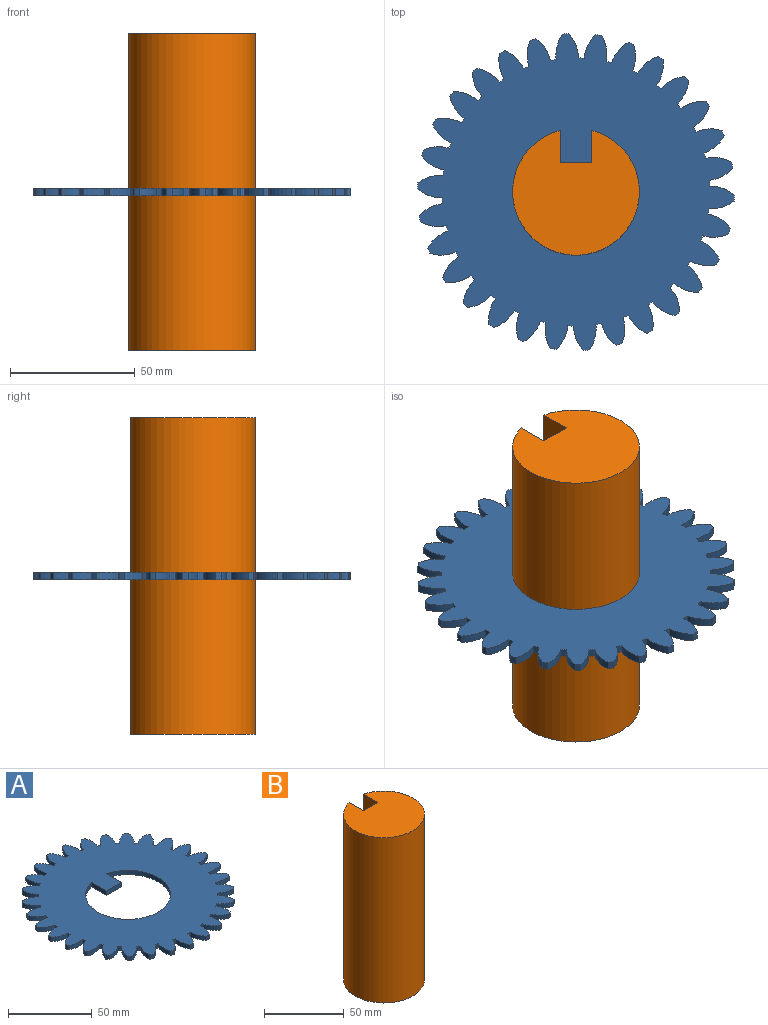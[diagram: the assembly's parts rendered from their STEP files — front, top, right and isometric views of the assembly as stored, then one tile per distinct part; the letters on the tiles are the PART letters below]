
ASSEMBLY  parts=2 mates=1
PART A: 126 faces, bbox 127x126.9x3.2 mm
  f0: cylinder r=25.4mm len=50.8mm, axis (0,0,-1), area 466mm2, adj f1,f123,f124,f125
  f1: plane 12.7x3.18mm, normal (-1,0,0), area 40.3mm2, adj f0,f2,f124,f125
  f2: plane 12.7x3.18mm, normal (0,-1,0), area 40.3mm2, adj f1,f123,f124,f125
  f3: cylinder r=14.61mm len=10.37mm, axis (0,0,-1), area 34.1mm2, adj f4,f122,f124,f125
  f4: cylinder r=53.72mm len=3.18mm, axis (0,0,-1), area 7.2mm2, adj f3,f5,f124,f125
  f5: cylinder r=14.61mm len=8.02mm, axis (0,0,-1), area 34.1mm2, adj f4,f6,f124,f125
  f6: cylinder r=63.5mm len=3.18mm, axis (0,0,-1), area 7.4mm2, adj f5,f7,f124,f125
  f7: cylinder r=14.61mm len=10.48mm, axis (0,0,-1), area 34.1mm2, adj f6,f8,f124,f125
  f8: cylinder r=53.72mm len=3.18mm, axis (0,0,-1), area 7.2mm2, adj f7,f9,f124,f125
  f9: cylinder r=14.61mm len=8.29mm, axis (0,0,-1), area 34.1mm2, adj f8,f10,f124,f125
  f10: cylinder r=63.5mm len=3.18mm, axis (0,0,-1), area 7.4mm2, adj f9,f11,f124,f125
  f11: cylinder r=14.61mm len=10.12mm, axis (0,0,-1), area 34.1mm2, adj f10,f12,f124,f125
  f12: cylinder r=53.72mm len=3.18mm, axis (0,0,-1), area 7.2mm2, adj f11,f13,f124,f125
  f13: cylinder r=14.61mm len=9.45mm, axis (0,0,-1), area 34.1mm2, adj f12,f14,f124,f125
  f14: cylinder r=63.5mm len=3.18mm, axis (0,0,-1), area 7.4mm2, adj f13,f15,f124,f125
  f15: cylinder r=14.61mm len=9.32mm, axis (0,0,-1), area 34.1mm2, adj f14,f16,f124,f125
  f16: cylinder r=53.72mm len=3.18mm, axis (0,0,-1), area 7.2mm2, adj f15,f17,f124,f125
  f17: cylinder r=14.61mm len=10.19mm, axis (0,0,-1), area 34.1mm2, adj f16,f18,f124,f125
  f18: cylinder r=63.5mm len=3.18mm, axis (0,0,-1), area 7.4mm2, adj f17,f19,f124,f125
  f19: cylinder r=14.61mm len=8.12mm, axis (0,0,-1), area 34.1mm2, adj f18,f20,f124,f125
  f20: cylinder r=53.72mm len=3.18mm, axis (0,0,-1), area 7.2mm2, adj f19,f21,f124,f125
  f21: cylinder r=14.61mm len=10.49mm, axis (0,0,-1), area 34.1mm2, adj f20,f22,f124,f125
  f22: cylinder r=63.5mm len=3.18mm, axis (0,0,-1), area 7.4mm2, adj f21,f23,f124,f125
  f23: cylinder r=14.61mm len=8.19mm, axis (0,0,-1), area 34.1mm2, adj f22,f24,f124,f125
  f24: cylinder r=53.72mm len=3.18mm, axis (0,0,-1), area 7.2mm2, adj f23,f25,f124,f125
  f25: cylinder r=14.61mm len=10.33mm, axis (0,0,-1), area 34.1mm2, adj f24,f26,f124,f125
  f26: cylinder r=63.5mm len=3.18mm, axis (0,0,-1), area 7.4mm2, adj f25,f27,f124,f125
  f27: cylinder r=14.61mm len=9.38mm, axis (0,0,-1), area 34.1mm2, adj f26,f28,f124,f125
  f28: cylinder r=53.72mm len=3.18mm, axis (0,0,-1), area 7.2mm2, adj f27,f29,f124,f125
  f29: cylinder r=14.61mm len=9.72mm, axis (0,0,-1), area 34.1mm2, adj f28,f30,f124,f125
  f30: cylinder r=63.5mm len=3.18mm, axis (0,0,-1), area 7.4mm2, adj f29,f31,f124,f125
  f31: cylinder r=14.61mm len=10.15mm, axis (0,0,-1), area 34.1mm2, adj f30,f32,f124,f125
  f32: cylinder r=53.72mm len=3.18mm, axis (0,0,-1), area 7.2mm2, adj f31,f33,f124,f125
  f33: cylinder r=14.61mm len=8.68mm, axis (0,0,-1), area 34.1mm2, adj f32,f34,f124,f125
  f34: cylinder r=63.5mm len=3.18mm, axis (0,0,-1), area 7.4mm2, adj f33,f35,f124,f125
  f35: cylinder r=14.61mm len=10.48mm, axis (0,0,-1), area 34.1mm2, adj f34,f36,f124,f125
  f36: cylinder r=53.72mm len=3.18mm, axis (0,0,-1), area 7.2mm2, adj f35,f37,f124,f125
  f37: cylinder r=14.61mm len=7.57mm, axis (0,0,-1), area 34.1mm2, adj f36,f38,f124,f125
  f38: cylinder r=63.5mm len=3.18mm, axis (0,0,-1), area 7.4mm2, adj f37,f39,f124,f125
  f39: cylinder r=14.61mm len=10.36mm, axis (0,0,-1), area 34.1mm2, adj f38,f40,f124,f125
  f40: cylinder r=53.72mm len=3.18mm, axis (0,0,-1), area 7.2mm2, adj f39,f41,f124,f125
  f41: cylinder r=14.61mm len=8.92mm, axis (0,0,-1), area 34.1mm2, adj f40,f42,f124,f125
  f42: cylinder r=63.5mm len=3.18mm, axis (0,0,-1), area 7.4mm2, adj f41,f43,f124,f125
  f43: cylinder r=14.61mm len=9.78mm, axis (0,0,-1), area 34.1mm2, adj f42,f44,f124,f125
  f44: cylinder r=53.72mm len=3.18mm, axis (0,0,-1), area 7.2mm2, adj f43,f45,f124,f125
  f45: cylinder r=14.61mm len=9.87mm, axis (0,0,-1), area 34.1mm2, adj f44,f46,f124,f125
  f46: cylinder r=63.5mm len=3.18mm, axis (0,0,-1), area 7.4mm2, adj f45,f47,f124,f125
  f47: cylinder r=14.61mm len=8.77mm, axis (0,0,-1), area 34.1mm2, adj f46,f48,f124,f125
  f48: cylinder r=53.72mm len=3.18mm, axis (0,0,-1), area 7.2mm2, adj f47,f49,f124,f125
  f49: cylinder r=14.61mm len=10.4mm, axis (0,0,-1), area 34.1mm2, adj f48,f50,f124,f125
  f50: cylinder r=63.5mm len=3.18mm, axis (0,0,-1), area 7.4mm2, adj f49,f51,f124,f125
  f51: cylinder r=14.61mm len=7.46mm, axis (0,0,-1), area 34.1mm2, adj f50,f52,f124,f125
  f52: cylinder r=53.72mm len=3.18mm, axis (0,0,-1), area 7.2mm2, adj f51,f53,f124,f125
  f53: cylinder r=14.61mm len=10.47mm, axis (0,0,-1), area 34.1mm2, adj f52,f54,f124,f125
  f54: cylinder r=63.5mm len=3.18mm, axis (0,0,-1), area 7.4mm2, adj f53,f55,f124,f125
  f55: cylinder r=14.61mm len=8.83mm, axis (0,0,-1), area 34.1mm2, adj f54,f56,f124,f125
  f56: cylinder r=53.72mm len=3.18mm, axis (0,0,-1), area 7.2mm2, adj f55,f57,f124,f125
  f57: cylinder r=14.61mm len=10.08mm, axis (0,0,-1), area 34.1mm2, adj f56,f58,f124,f125
  f58: cylinder r=63.5mm len=3.18mm, axis (0,0,-1), area 7.4mm2, adj f57,f59,f124,f125
  f59: cylinder r=14.61mm len=9.82mm, axis (0,0,-1), area 34.1mm2, adj f58,f60,f124,f125
  f60: cylinder r=53.72mm len=3.18mm, axis (0,0,-1), area 7.2mm2, adj f59,f61,f124,f125
  f61: cylinder r=14.61mm len=9.25mm, axis (0,0,-1), area 34.1mm2, adj f60,f62,f124,f125
  f62: cylinder r=63.5mm len=3.18mm, axis (0,0,-1), area 7.4mm2, adj f61,f63,f124,f125
  f63: cylinder r=14.61mm len=10.37mm, axis (0,0,-1), area 34.1mm2, adj f62,f64,f124,f125
  f64: cylinder r=53.72mm len=3.18mm, axis (0,0,-1), area 7.2mm2, adj f63,f65,f124,f125
  f65: cylinder r=14.61mm len=8.02mm, axis (0,0,-1), area 34.1mm2, adj f64,f66,f124,f125
  f66: cylinder r=63.5mm len=3.18mm, axis (0,0,-1), area 7.4mm2, adj f65,f67,f124,f125
  f67: cylinder r=14.61mm len=10.48mm, axis (0,0,-1), area 34.1mm2, adj f66,f68,f124,f125
  f68: cylinder r=53.72mm len=3.18mm, axis (0,0,-1), area 7.2mm2, adj f67,f69,f124,f125
  f69: cylinder r=14.61mm len=8.29mm, axis (0,0,-1), area 34.1mm2, adj f68,f70,f124,f125
  f70: cylinder r=63.5mm len=3.18mm, axis (0,0,-1), area 7.4mm2, adj f69,f71,f124,f125
  f71: cylinder r=14.61mm len=10.12mm, axis (0,0,-1), area 34.1mm2, adj f70,f72,f124,f125
  f72: cylinder r=53.72mm len=3.18mm, axis (0,0,-1), area 7.2mm2, adj f71,f73,f124,f125
  f73: cylinder r=14.61mm len=9.45mm, axis (0,0,-1), area 34.1mm2, adj f72,f74,f124,f125
  f74: cylinder r=63.5mm len=3.18mm, axis (0,0,-1), area 7.4mm2, adj f73,f75,f124,f125
  f75: cylinder r=14.61mm len=9.32mm, axis (0,0,-1), area 34.1mm2, adj f74,f76,f124,f125
  f76: cylinder r=53.72mm len=3.18mm, axis (0,0,-1), area 7.2mm2, adj f75,f77,f124,f125
  f77: cylinder r=14.61mm len=10.19mm, axis (0,0,-1), area 34.1mm2, adj f76,f78,f124,f125
  f78: cylinder r=63.5mm len=3.18mm, axis (0,0,-1), area 7.4mm2, adj f77,f79,f124,f125
  f79: cylinder r=14.61mm len=8.12mm, axis (0,0,-1), area 34.1mm2, adj f78,f80,f124,f125
  f80: cylinder r=53.72mm len=3.18mm, axis (0,0,-1), area 7.2mm2, adj f79,f81,f124,f125
  f81: cylinder r=14.61mm len=10.49mm, axis (0,0,-1), area 34.1mm2, adj f80,f82,f124,f125
  f82: cylinder r=63.5mm len=3.18mm, axis (0,0,-1), area 7.4mm2, adj f81,f83,f124,f125
  f83: cylinder r=14.61mm len=8.19mm, axis (0,0,-1), area 34.1mm2, adj f82,f84,f124,f125
  f84: cylinder r=53.72mm len=3.18mm, axis (0,0,-1), area 7.2mm2, adj f83,f85,f124,f125
  f85: cylinder r=14.61mm len=10.33mm, axis (0,0,-1), area 34.1mm2, adj f84,f86,f124,f125
  f86: cylinder r=63.5mm len=3.18mm, axis (0,0,-1), area 7.4mm2, adj f85,f87,f124,f125
  f87: cylinder r=14.61mm len=9.38mm, axis (0,0,-1), area 34.1mm2, adj f86,f88,f124,f125
  f88: cylinder r=53.72mm len=3.18mm, axis (0,0,-1), area 7.2mm2, adj f87,f89,f124,f125
  f89: cylinder r=14.61mm len=9.72mm, axis (0,0,-1), area 34.1mm2, adj f88,f90,f124,f125
  f90: cylinder r=63.5mm len=3.18mm, axis (0,0,-1), area 7.4mm2, adj f89,f91,f124,f125
  f91: cylinder r=14.61mm len=10.15mm, axis (0,0,-1), area 34.1mm2, adj f90,f92,f124,f125
  f92: cylinder r=53.72mm len=3.18mm, axis (0,0,-1), area 7.2mm2, adj f91,f93,f124,f125
  f93: cylinder r=14.61mm len=8.68mm, axis (0,0,-1), area 34.1mm2, adj f92,f94,f124,f125
  f94: cylinder r=63.5mm len=3.18mm, axis (0,0,-1), area 7.4mm2, adj f93,f95,f124,f125
  f95: cylinder r=14.61mm len=10.48mm, axis (0,0,-1), area 34.1mm2, adj f94,f96,f124,f125
  f96: cylinder r=53.72mm len=3.18mm, axis (0,0,-1), area 7.2mm2, adj f95,f97,f124,f125
  f97: cylinder r=14.61mm len=7.57mm, axis (0,0,-1), area 34.1mm2, adj f96,f98,f124,f125
  f98: cylinder r=63.5mm len=3.18mm, axis (0,0,-1), area 7.4mm2, adj f97,f99,f124,f125
  f99: cylinder r=14.61mm len=10.36mm, axis (0,0,-1), area 34.1mm2, adj f98,f100,f124,f125
  f100: cylinder r=53.72mm len=3.18mm, axis (0,0,-1), area 7.2mm2, adj f99,f101,f124,f125
  f101: cylinder r=14.61mm len=8.92mm, axis (0,0,-1), area 34.1mm2, adj f100,f102,f124,f125
  f102: cylinder r=63.5mm len=3.18mm, axis (0,0,-1), area 7.4mm2, adj f101,f103,f124,f125
  f103: cylinder r=14.61mm len=9.78mm, axis (0,0,-1), area 34.1mm2, adj f102,f104,f124,f125
  f104: cylinder r=53.72mm len=3.18mm, axis (0,0,-1), area 7.2mm2, adj f103,f105,f124,f125
  f105: cylinder r=14.61mm len=9.87mm, axis (0,0,-1), area 34.1mm2, adj f104,f106,f124,f125
  f106: cylinder r=63.5mm len=3.18mm, axis (0,0,-1), area 7.4mm2, adj f105,f107,f124,f125
  f107: cylinder r=14.61mm len=8.77mm, axis (0,0,-1), area 34.1mm2, adj f106,f108,f124,f125
  f108: cylinder r=53.72mm len=3.18mm, axis (0,0,-1), area 7.2mm2, adj f107,f109,f124,f125
  f109: cylinder r=14.61mm len=10.4mm, axis (0,0,-1), area 34.1mm2, adj f108,f110,f124,f125
  f110: cylinder r=63.5mm len=3.18mm, axis (0,0,-1), area 7.4mm2, adj f109,f111,f124,f125
  f111: cylinder r=14.61mm len=7.46mm, axis (0,0,-1), area 34.1mm2, adj f110,f112,f124,f125
  f112: cylinder r=53.72mm len=3.18mm, axis (0,0,-1), area 7.2mm2, adj f111,f113,f124,f125
  f113: cylinder r=14.61mm len=10.47mm, axis (0,0,-1), area 34.1mm2, adj f112,f114,f124,f125
  f114: cylinder r=63.5mm len=3.18mm, axis (0,0,-1), area 7.4mm2, adj f113,f115,f124,f125
  f115: cylinder r=14.61mm len=8.83mm, axis (0,0,-1), area 34.1mm2, adj f114,f116,f124,f125
  f116: cylinder r=53.72mm len=3.18mm, axis (0,0,-1), area 7.2mm2, adj f115,f117,f124,f125
  f117: cylinder r=14.61mm len=10.08mm, axis (0,0,-1), area 34.1mm2, adj f116,f118,f124,f125
  f118: cylinder r=63.5mm len=3.18mm, axis (0,0,-1), area 7.4mm2, adj f117,f119,f124,f125
  f119: cylinder r=14.61mm len=9.82mm, axis (0,0,-1), area 34.1mm2, adj f118,f120,f124,f125
  f120: cylinder r=53.72mm len=3.18mm, axis (0,0,-1), area 7.2mm2, adj f119,f121,f124,f125
  f121: cylinder r=14.61mm len=9.25mm, axis (0,0,-1), area 34.1mm2, adj f120,f122,f124,f125
  f122: cylinder r=63.5mm len=3.18mm, axis (0,0,-1), area 7.4mm2, adj f3,f121,f124,f125
  f123: plane 12.7x3.18mm, normal (1,0,0), area 40.3mm2, adj f0,f2,f124,f125
  f124: plane 126.97x126.86mm, normal (0,0,1), area 9274.2mm2, adj f0,f1,f2,f3,f4,f5,f6,f7
  f125: plane 126.97x126.86mm, normal (0,0,-1), area 9274.2mm2, adj f0,f1,f2,f3,f4,f5,f6,f7
PART B: 6 faces, bbox 50.8x50x127 mm
  f0: plane 127x12.7mm, normal (1,0,0), area 1612.9mm2, adj f1,f3,f4,f5
  f1: cylinder r=25.4mm len=127mm, axis (0,0,-1), area 18638.1mm2, adj f0,f2,f4,f5
  f2: plane 127x12.7mm, normal (-1,0,0), area 1612.9mm2, adj f1,f3,f4,f5
  f3: plane 127x12.7mm, normal (0,1,0), area 1612.9mm2, adj f0,f2,f4,f5
  f4: plane 50.8x49.99mm, normal (0,0,1), area 1858.7mm2, adj f0,f1,f2,f3
  f5: plane 50.8x49.99mm, normal (0,0,-1), area 1858.7mm2, adj f0,f1,f2,f3
PLACE A rot(axis=(-0.21,0.73,-0.66),0deg) t=(-68.99,-85.71,176.84)mm
PLACE B rot(axis=(-0.21,0.73,-0.66),0deg) t=(-68.99,-85.71,114.93)mm
MATE slider B.f1 <-> A.f0  axis (0,0,-1) through (-68.99,-85.71,178.43)mm
